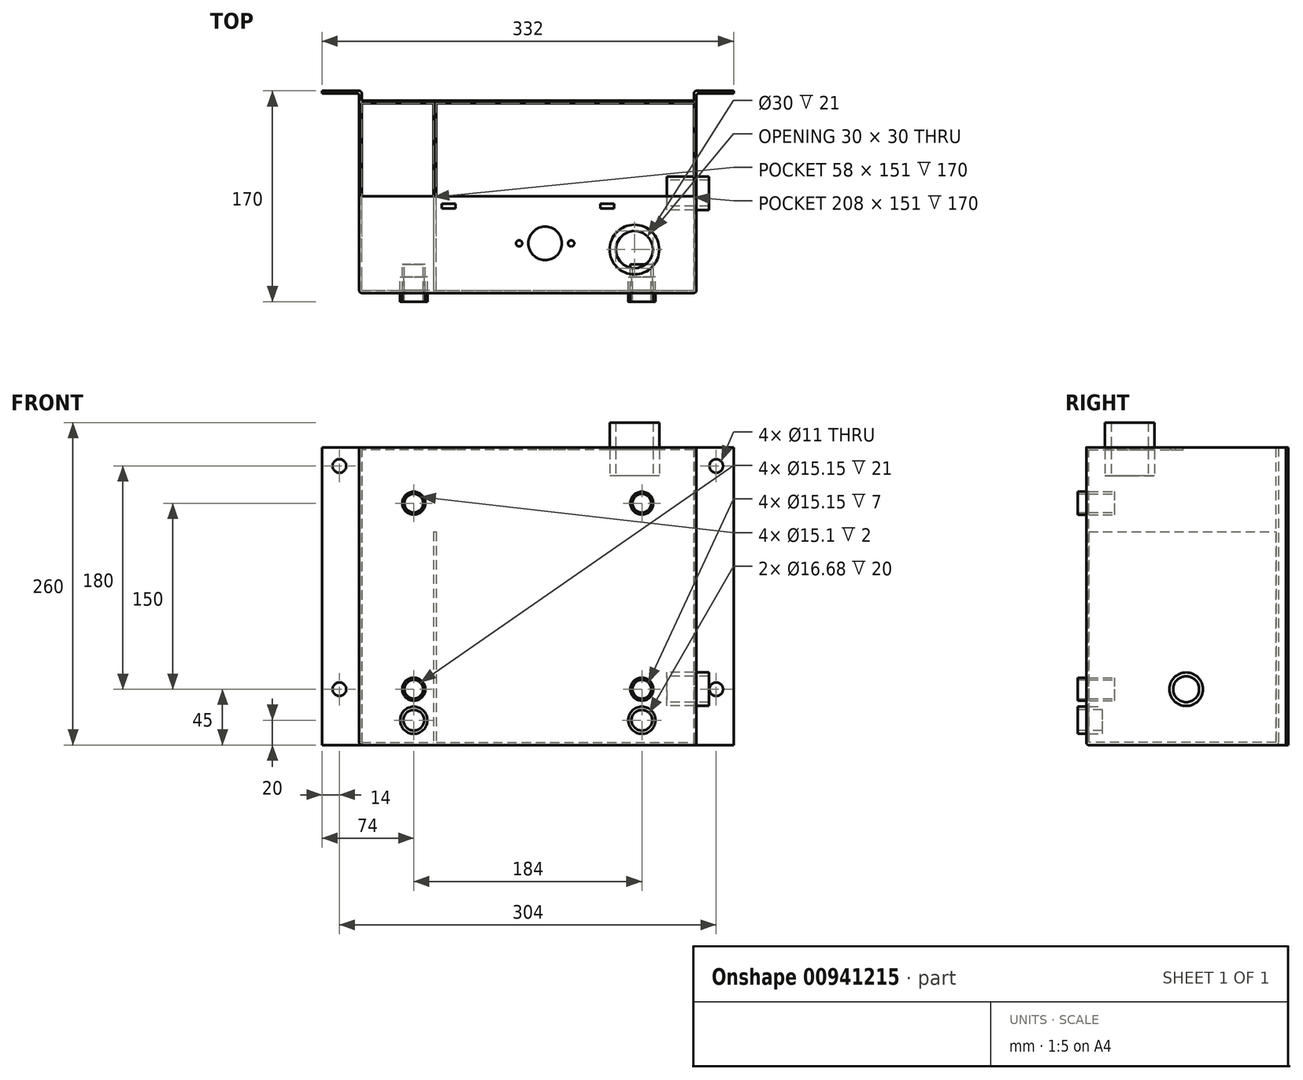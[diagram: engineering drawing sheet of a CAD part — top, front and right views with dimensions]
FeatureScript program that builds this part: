
annotation { "Feature Type Name" : "Feature", "Feature Type Description" : "" }
export const myFeature = defineFeature(function(context is Context, id is Id, definition is map)
    precondition{}
    {
        {
            var Q0;
            Q0=qCreatedBy(makeId("Top.planeOp"),FACE);
            var sketch = newSketch(context, id + "F0", { "sketchPlane" : qUnion([Q0])});
            skLineSegment(sketch, "E0", {"start": v(0, 0) * mm, "end": v(134, 0) * mm});
            skLineSegment(sketch, "E1", {"start": v(136, 0) * mm, "end": v(136, 4) * mm});
            skLineSegment(sketch, "E2", {"start": v(138, 6) * mm, "end": v(166, 6) * mm});
            skPoint(sketch, "E3.visualSharp", {"position": v(136, 6) * mm});
            skArc(sketch, "E3.filletArc", {"start": v(138, 6) * mm, "mid": v(136.59, 5.41) * mm, "end": v(136, 4) * mm});
            skLineSegment(sketch, "E4", {"start": v(136, 0) * mm, "end": v(136, -153) * mm});
            skLineSegment(sketch, "E5", {"start": v(134, -155) * mm, "end": v(0, -155) * mm});
            skPoint(sketch, "E6", {"position": v(0, -2) * mm});
            skLineSegment(sketch, "E7", {"start": v(0, -2) * mm, "end": v(134, -2) * mm});
            skLineSegment(sketch, "E8", {"start": v(134, -2) * mm, "end": v(134, -151) * mm});
            skLineSegment(sketch, "E9", {"start": v(132, -153) * mm, "end": v(0, -153) * mm});
            skLineSegment(sketch, "E10", {"start": v(166, 6) * mm, "end": v(166, 8) * mm});
            skLineSegment(sketch, "E11", {"start": v(134, 0) * mm, "end": v(134, 6) * mm});
            skLineSegment(sketch, "E12", {"start": v(136, 8) * mm, "end": v(166, 8) * mm});
            skPoint(sketch, "E13.visualSharp", {"position": v(134, 8) * mm});
            skArc(sketch, "E13.filletArc", {"start": v(136, 8) * mm, "mid": v(134.59, 7.41) * mm, "end": v(134, 6) * mm});
            skArc(sketch, "E14.MirrorCS", {"start": v(-138, 6) * mm, "mid": v(-136.59, 5.41) * mm, "end": v(-136, 4) * mm});
            skLineSegment(sketch, "E15.MirrorCS", {"start": v(-134, 0) * mm, "end": v(-134, 6) * mm});
            skArc(sketch, "E16.MirrorCS", {"start": v(-136, 8) * mm, "mid": v(-134.59, 7.41) * mm, "end": v(-134, 6) * mm});
            skLineSegment(sketch, "E17.MirrorCS", {"start": v(-136, 0) * mm, "end": v(-136, 4) * mm});
            skLineSegment(sketch, "E18.MirrorCS", {"start": v(-166, 6) * mm, "end": v(-166, 8) * mm});
            skLineSegment(sketch, "E19.MirrorCS", {"start": v(-138, 6) * mm, "end": v(-166, 6) * mm});
            skLineSegment(sketch, "E20.MirrorCS", {"start": v(-134, -2) * mm, "end": v(-134, -151) * mm});
            skLineSegment(sketch, "E21.MirrorCS", {"start": v(-132, -153) * mm, "end": v(0, -153) * mm});
            skPoint(sketch, "E22.MirrorP", {"position": v(-134, 8) * mm});
            skLineSegment(sketch, "E23.MirrorCS", {"start": v(-136, 8) * mm, "end": v(-166, 8) * mm});
            skLineSegment(sketch, "E24.MirrorCS", {"start": v(0, 0) * mm, "end": v(-134, 0) * mm});
            skLineSegment(sketch, "E25.MirrorCS", {"start": v(-134, -155) * mm, "end": v(0, -155) * mm});
            skLineSegment(sketch, "E26.MirrorCS", {"start": v(0, -2) * mm, "end": v(-134, -2) * mm});
            skLineSegment(sketch, "E27.MirrorCS", {"start": v(-136, 0) * mm, "end": v(-136, -153) * mm});
            skPoint(sketch, "E28.visualSharp", {"position": v(-136, -155) * mm});
            skArc(sketch, "E28.filletArc", {"start": v(-136, -153) * mm, "mid": v(-135.41, -154.41) * mm, "end": v(-134, -155) * mm});
            skArc(sketch, "E29.filletArc", {"start": v(-134, -151) * mm, "mid": v(-133.41, -152.41) * mm, "end": v(-132, -153) * mm});
            skPoint(sketch, "E30.visualSharp", {"position": v(136, -155) * mm});
            skArc(sketch, "E30.filletArc", {"start": v(134, -155) * mm, "mid": v(135.41, -154.41) * mm, "end": v(136, -153) * mm});
            skArc(sketch, "E31.filletArc", {"start": v(132, -153) * mm, "mid": v(133.41, -152.41) * mm, "end": v(134, -151) * mm});
            skSolve(sketch);
        }
        {
            var Q0;
            Q0=makeQuery(id+"F0.imprint","IMPRINT",FACE,{"disambiguationData":[TD([[makeQuery(id+"F0.imprint","IMPRINT",EDGE,{"derivedFrom":sQuery(id+"F0.wireOp",EDGE,"E7")}),-1.0]])]});
            var Q1;
            Q1=makeQuery(id+"F0.imprint","IMPRINT",FACE,{"disambiguationData":[TD([[makeQuery(id+"F0.imprint","IMPRINT",EDGE,{"derivedFrom":sQuery(id+"F0.wireOp",EDGE,"E0")}),-1.0]])]});
            var Q2;
            Q2=makeQuery(id+"F0.imprint","IMPRINT",FACE,{"disambiguationData":[TD([[makeQuery(id+"F0.imprint","IMPRINT",EDGE,{"derivedFrom":sQuery(id+"F0.wireOp",EDGE,"AYROce98-IXZU-P0DJ-6LKk-YyaPTNVELOtw")}),1.0]])]});
            extrude(context, id + "F1", {"entities" : qUnion([Q0, Q1, Q2]), "depth" : 240 * mm, "offsetDistance" : 25 * mm});
        }
        {
            var Q0;
            Q0=makeQuery(id+"F1.opExtrude","CAP_FACE",FACE,{"disambiguationData":[OSD([sQuery(id+"F0.wireOp",EDGE,"E0"),sQuery(id+"F0.wireOp",EDGE,"E1"),sQuery(id+"F0.wireOp",EDGE,"E2"),sQuery(id+"F0.wireOp",EDGE,"E3.filletArc"),sQuery(id+"F0.wireOp",EDGE,"E4"),sQuery(id+"F0.wireOp",EDGE,"E5"),sQuery(id+"F0.wireOp",EDGE,"E10"),sQuery(id+"F0.wireOp",EDGE,"E11"),sQuery(id+"F0.wireOp",EDGE,"E12"),sQuery(id+"F0.wireOp",EDGE,"E13.filletArc"),sQuery(id+"F0.wireOp",EDGE,"E14.MirrorCS"),sQuery(id+"F0.wireOp",EDGE,"E15.MirrorCS"),sQuery(id+"F0.wireOp",EDGE,"E16.MirrorCS"),sQuery(id+"F0.wireOp",EDGE,"E17.MirrorCS"),sQuery(id+"F0.wireOp",EDGE,"E18.MirrorCS"),sQuery(id+"F0.wireOp",EDGE,"E19.MirrorCS"),sQuery(id+"F0.wireOp",EDGE,"E23.MirrorCS"),sQuery(id+"F0.wireOp",EDGE,"E24.MirrorCS"),sQuery(id+"F0.wireOp",EDGE,"E25.MirrorCS"),sQuery(id+"F0.wireOp",EDGE,"E27.MirrorCS"),sQuery(id+"F0.wireOp",EDGE,"E28.filletArc"),sQuery(id+"F0.wireOp",EDGE,"E30.filletArc")])],"isStart":false});
            var sketch = newSketch(context, id + "F2", { "sketchPlane" : qUnion([Q0])});
            skPoint(sketch, "E32", {"position": v(-134, -2) * mm});
            skLineSegment(sketch, "E33.bottom", {"start": v(-134, -2) * mm, "end": v(134, -2) * mm});
            skLineSegment(sketch, "E33.top", {"start": v(-134, -153) * mm, "end": v(134, -153) * mm});
            skLineSegment(sketch, "E33.left", {"start": v(-134, -2) * mm, "end": v(-134, -153) * mm});
            skLineSegment(sketch, "E33.right", {"start": v(134, -2) * mm, "end": v(134, -153) * mm});
            skSolve(sketch);
        }
        {
            var Q0;
            Q0=makeQuery(id+"F2.imprint","IMPRINT",FACE,{"disambiguationData":[TD([[makeQuery(id+"F2.imprint","IMPRINT",EDGE,{"derivedFrom":sQuery(id+"F2.wireOp",EDGE,"E33.bottom")}),-1.0]])]});
            extrude(context, id + "F3", {"entities" : qUnion([Q0]), "operationType" : NewBodyOperationType.REMOVE, "oppositeDirection" : true, "depth" : 238 * mm, "offsetDistance" : 25 * mm});
        }
        {
            var Q0;
            Q0=makeQuery(id+"F1.opExtrude","SWEPT_FACE",FACE,{"disambiguationData":[OSD([sQuery(id+"F0.wireOp",EDGE,"E19.MirrorCS")])]});
            var sketch = newSketch(context, id + "F4", { "sketchPlane" : qUnion([Q0])});
            skPoint(sketch, "E34", {"position": v(-152, 45) * mm});
            skPoint(sketch, "E35", {"position": v(-152, 225) * mm});
            skSolve(sketch);
        }
        {
            var Q0;
            Q0=sQuery(id+"F4.wireOp",VERTEX,"E35");
            var Q1;
            Q1=sQuery(id+"F4.wireOp",VERTEX,"E34");
            var Q2;
            Q2=makeQuery(id+"F1.opExtrude","SWEPT_BODY",BODY,{"disambiguationData":[OSD([sQuery(id+"F0.wireOp",EDGE,"E0"),sQuery(id+"F0.wireOp",EDGE,"E1"),sQuery(id+"F0.wireOp",EDGE,"E2"),sQuery(id+"F0.wireOp",EDGE,"E3.filletArc"),sQuery(id+"F0.wireOp",EDGE,"E4"),sQuery(id+"F0.wireOp",EDGE,"E5"),sQuery(id+"F0.wireOp",EDGE,"E10"),sQuery(id+"F0.wireOp",EDGE,"E11"),sQuery(id+"F0.wireOp",EDGE,"E12"),sQuery(id+"F0.wireOp",EDGE,"E13.filletArc"),sQuery(id+"F0.wireOp",EDGE,"E14.MirrorCS"),sQuery(id+"F0.wireOp",EDGE,"E15.MirrorCS"),sQuery(id+"F0.wireOp",EDGE,"E16.MirrorCS"),sQuery(id+"F0.wireOp",EDGE,"E17.MirrorCS"),sQuery(id+"F0.wireOp",EDGE,"E18.MirrorCS"),sQuery(id+"F0.wireOp",EDGE,"E19.MirrorCS"),sQuery(id+"F0.wireOp",EDGE,"E23.MirrorCS"),sQuery(id+"F0.wireOp",EDGE,"E24.MirrorCS"),sQuery(id+"F0.wireOp",EDGE,"E25.MirrorCS"),sQuery(id+"F0.wireOp",EDGE,"E27.MirrorCS"),sQuery(id+"F0.wireOp",EDGE,"E28.filletArc"),sQuery(id+"F0.wireOp",EDGE,"E30.filletArc")])]});
            hole(context, id + "F5", {"style" : HoleStyle.SIMPLE, "endStyle" : HoleEndStyle.THROUGH, "holeDiameter" : 11 * mm, "majorDiameter" : 4 * mm, "isTappedThrough" : true, "tappedDepth" : 5.5 * mm, "tapClearance" : 3, "locations" : qUnion([Q0, Q1]), "scope" : qUnion([Q2])});
        }
        {
            var Q0;
            Q0=makeQuery(id+"F1.opExtrude","SWEPT_FACE",FACE,{"disambiguationData":[OSD([sQuery(id+"F0.wireOp",EDGE,"E2")])]});
            var sketch = newSketch(context, id + "F6", { "sketchPlane" : qUnion([Q0])});
            skPoint(sketch, "E36", {"position": v(152, 225) * mm});
            skPoint(sketch, "E37", {"position": v(152, 45) * mm});
            skSolve(sketch);
        }
        {
            var Q0;
            Q0=sQuery(id+"F6.wireOp",VERTEX,"E36");
            var Q1;
            Q1=sQuery(id+"F6.wireOp",VERTEX,"E37");
            var Q2;
            Q2=makeQuery(id+"F1.opExtrude","SWEPT_BODY",BODY,{"disambiguationData":[OSD([sQuery(id+"F0.wireOp",EDGE,"E0"),sQuery(id+"F0.wireOp",EDGE,"E1"),sQuery(id+"F0.wireOp",EDGE,"E2"),sQuery(id+"F0.wireOp",EDGE,"E3.filletArc"),sQuery(id+"F0.wireOp",EDGE,"E4"),sQuery(id+"F0.wireOp",EDGE,"E5"),sQuery(id+"F0.wireOp",EDGE,"E10"),sQuery(id+"F0.wireOp",EDGE,"E11"),sQuery(id+"F0.wireOp",EDGE,"E12"),sQuery(id+"F0.wireOp",EDGE,"E13.filletArc"),sQuery(id+"F0.wireOp",EDGE,"E14.MirrorCS"),sQuery(id+"F0.wireOp",EDGE,"E15.MirrorCS"),sQuery(id+"F0.wireOp",EDGE,"E16.MirrorCS"),sQuery(id+"F0.wireOp",EDGE,"E17.MirrorCS"),sQuery(id+"F0.wireOp",EDGE,"E18.MirrorCS"),sQuery(id+"F0.wireOp",EDGE,"E19.MirrorCS"),sQuery(id+"F0.wireOp",EDGE,"E23.MirrorCS"),sQuery(id+"F0.wireOp",EDGE,"E24.MirrorCS"),sQuery(id+"F0.wireOp",EDGE,"E25.MirrorCS"),sQuery(id+"F0.wireOp",EDGE,"E27.MirrorCS"),sQuery(id+"F0.wireOp",EDGE,"E28.filletArc"),sQuery(id+"F0.wireOp",EDGE,"E30.filletArc")])]});
            hole(context, id + "F7", {"style" : HoleStyle.SIMPLE, "endStyle" : HoleEndStyle.THROUGH, "holeDiameter" : 11 * mm, "majorDiameter" : 5 * mm, "isTappedThrough" : true, "tappedDepth" : 5.5 * mm, "tapClearance" : 3, "locations" : qUnion([Q0, Q1]), "scope" : qUnion([Q2])});
        }
        {
            var Q0;
            Q0=makeQuery(id+"F1.opExtrude","SWEPT_FACE",FACE,{"disambiguationData":[OSD([sQuery(id+"F0.wireOp",EDGE,"E5"),sQuery(id+"F0.wireOp",EDGE,"E25.MirrorCS")])]});
            var sketch = newSketch(context, id + "F8", { "sketchPlane" : qUnion([Q0])});
            skPoint(sketch, "E38", {"position": v(-92, 195) * mm});
            skPoint(sketch, "E39", {"position": v(-92, 45) * mm});
            skLineSegment(sketch, "E40", {"start": v(0, 240) * mm, "end": v(0, 0) * mm});
            skPoint(sketch, "E41.MirrorP", {"position": v(92, 45) * mm});
            skPoint(sketch, "E42.MirrorP", {"position": v(92, 195) * mm});
            skCircle(sketch, "E43", {"center": v(-92, 195) * mm, "radius": 9.25 * mm});
            skCircle(sketch, "E44", {"center": v(-92, 195) * mm, "radius": 7.58 * mm});
            skCircle(sketch, "E45", {"center": v(-92, 45) * mm, "radius": 9.25 * mm});
            skCircle(sketch, "E46", {"center": v(-92, 45) * mm, "radius": 7.58 * mm});
            skCircle(sketch, "E47", {"center": v(92, 195) * mm, "radius": 9.25 * mm});
            skCircle(sketch, "E48", {"center": v(92, 195) * mm, "radius": 7.58 * mm});
            skCircle(sketch, "E49", {"center": v(92, 45) * mm, "radius": 9.25 * mm});
            skCircle(sketch, "E50", {"center": v(92, 45) * mm, "radius": 7.58 * mm});
            skSolve(sketch);
        }
        {
            var Q0;
            Q0=makeQuery(id+"F8.imprint","IMPRINT",FACE,{"disambiguationData":[TD([[makeQuery(id+"F8.imprint","IMPRINT",EDGE,{"derivedFrom":sQuery(id+"F8.wireOp",EDGE,"E43")}),1.0]])]});
            var Q1;
            Q1=makeQuery(id+"F8.imprint","IMPRINT",FACE,{"disambiguationData":[TD([[makeQuery(id+"F8.imprint","IMPRINT",EDGE,{"derivedFrom":sQuery(id+"F8.wireOp",EDGE,"E45")}),1.0]])]});
            var Q2;
            Q2=makeQuery(id+"F8.imprint","IMPRINT",FACE,{"disambiguationData":[TD([[makeQuery(id+"F8.imprint","IMPRINT",EDGE,{"derivedFrom":sQuery(id+"F8.wireOp",EDGE,"E47")}),1.0]])]});
            var Q3;
            Q3=makeQuery(id+"F8.imprint","IMPRINT",FACE,{"disambiguationData":[TD([[makeQuery(id+"F8.imprint","IMPRINT",EDGE,{"derivedFrom":sQuery(id+"F8.wireOp",EDGE,"E49")}),1.0]])]});
            extrude(context, id + "F9", {"entities" : qUnion([Q0, Q1, Q2, Q3]), "operationType" : NewBodyOperationType.ADD, "depth" : 7 * mm, "offsetDistance" : 25 * mm, "hasSecondDirection" : true, "secondDirectionOppositeDirection" : true, "secondDirectionDepth" : 23 * mm});
        }
        {
            var Q0;
            {var subQ1=sQuery(id+"F0.wireOp",EDGE,"E28.filletArc");var subQ3=sQuery(id+"F0.wireOp",EDGE,"E25.MirrorCS");var subQ16=sQuery(id+"F0.wireOp",EDGE,"E5");Q0=makeQuery(id+"F9.boolean.opBoolean","SPLIT",FACE,{"disambiguationData":[TD([makeQuery(id+"F1.opExtrude","SWEPT_FACE",FACE,{"disambiguationData":[OSD([subQ1])]})])],"derivedFrom":makeQuery(id+"F1.opExtrude","SWEPT_FACE",FACE,{"disambiguationData":[OSD([subQ16,subQ3])]})});}
            var sketch = newSketch(context, id + "F10", { "sketchPlane" : qUnion([Q0])});
            skCircle(sketch, "E51", {"center": v(-92, 195) * mm, "radius": 7.55 * mm});
            skCircle(sketch, "E52", {"center": v(-92, 45) * mm, "radius": 7.55 * mm});
            skCircle(sketch, "E53", {"center": v(92, 195) * mm, "radius": 7.55 * mm});
            skCircle(sketch, "E54", {"center": v(92, 45) * mm, "radius": 7.55 * mm});
            skSolve(sketch);
        }
        {
            var Q0;
            Q0=makeQuery(id+"F10.imprint","IMPRINT",FACE,{"disambiguationData":[TD([[makeQuery(id+"F10.imprint","IMPRINT",EDGE,{"derivedFrom":sQuery(id+"F10.wireOp",EDGE,"E51")}),1.0]])]});
            var Q1;
            Q1=makeQuery(id+"F10.imprint","IMPRINT",FACE,{"disambiguationData":[TD([[makeQuery(id+"F10.imprint","IMPRINT",EDGE,{"derivedFrom":sQuery(id+"F10.wireOp",EDGE,"E52")}),1.0]])]});
            var Q2;
            Q2=makeQuery(id+"F10.imprint","IMPRINT",FACE,{"disambiguationData":[TD([[makeQuery(id+"F10.imprint","IMPRINT",EDGE,{"derivedFrom":sQuery(id+"F10.wireOp",EDGE,"E54")}),1.0]])]});
            var Q3;
            Q3=makeQuery(id+"F10.imprint","IMPRINT",FACE,{"disambiguationData":[TD([[makeQuery(id+"F10.imprint","IMPRINT",EDGE,{"derivedFrom":sQuery(id+"F10.wireOp",EDGE,"E53")}),1.0]])]});
            extrude(context, id + "F11", {"entities" : qUnion([Q0, Q1, Q2, Q3]), "operationType" : NewBodyOperationType.REMOVE, "oppositeDirection" : true, "depth" : 25 * mm, "offsetDistance" : 25 * mm});
        }
        {
            var Q0;
            Q0=makeQuery(id+"F1.opExtrude","SWEPT_FACE",FACE,{"disambiguationData":[OSD([sQuery(id+"F0.wireOp",EDGE,"E1"),sQuery(id+"F0.wireOp",EDGE,"E4")])]});
            var sketch = newSketch(context, id + "F12", { "sketchPlane" : qUnion([Q0])});
            skPoint(sketch, "E55.endSnap0", {"position": v(-74.5, 0) * mm});
            skCircle(sketch, "E56", {"center": v(-74.5, 45) * mm, "radius": 13.5 * mm});
            skCircle(sketch, "E57", {"center": v(-74.5, 45) * mm, "radius": 10.48 * mm});
            skSolve(sketch);
        }
        {
            var Q0;
            Q0=makeQuery(id+"F12.imprint","IMPRINT",FACE,{"disambiguationData":[TD([[makeQuery(id+"F12.imprint","IMPRINT",EDGE,{"derivedFrom":sQuery(id+"F12.wireOp",EDGE,"E56")}),1.0]])]});
            extrude(context, id + "F13", {"entities" : qUnion([Q0]), "operationType" : NewBodyOperationType.ADD, "depth" : 10 * mm, "offsetDistance" : 25 * mm, "hasSecondDirection" : true, "secondDirectionOppositeDirection" : true, "secondDirectionDepth" : 24 * mm});
        }
        {
            var Q0;
            {var subQ17=sQuery(id+"F0.wireOp",EDGE,"E4");var subQ18=sQuery(id+"F0.wireOp",EDGE,"E3.filletArc");var subQ20=sQuery(id+"F0.wireOp",EDGE,"E1");Q0=makeQuery(id+"F13.boolean.opBoolean","SPLIT",FACE,{"disambiguationData":[TD([makeQuery(id+"F1.opExtrude","SWEPT_FACE",FACE,{"disambiguationData":[OSD([subQ18])]})])],"derivedFrom":makeQuery(id+"F1.opExtrude","SWEPT_FACE",FACE,{"disambiguationData":[OSD([subQ20,subQ17])]})});}
            var sketch = newSketch(context, id + "F14", { "sketchPlane" : qUnion([Q0])});
            skCircle(sketch, "E58", {"center": v(-74.5, 45) * mm, "radius": 10.47 * mm});
            skSolve(sketch);
        }
        {
            var Q0;
            Q0=makeQuery(id+"F14.imprint","IMPRINT",FACE,{"disambiguationData":[TD([[makeQuery(id+"F14.imprint","IMPRINT",EDGE,{"derivedFrom":sQuery(id+"F14.wireOp",EDGE,"E58")}),1.0]])]});
            extrude(context, id + "F15", {"entities" : qUnion([Q0]), "operationType" : NewBodyOperationType.REMOVE, "oppositeDirection" : true, "depth" : 25 * mm, "offsetDistance" : 25 * mm});
        }
        {
            var Q0;
            Q0=makeQuery(id+"F3.boolean.opBoolean","COPY",FACE,{"derivedFrom":makeQuery(id+"F3.opExtrude","CAP_FACE",FACE,{"disambiguationData":[OSD([sQuery(id+"F2.wireOp",EDGE,"E33.bottom"),sQuery(id+"F2.wireOp",EDGE,"E33.top"),sQuery(id+"F2.wireOp",EDGE,"E33.left"),sQuery(id+"F2.wireOp",EDGE,"E33.right")])],"isStart":false})});
            var sketch = newSketch(context, id + "F16", { "sketchPlane" : qUnion([Q0])});
            skPoint(sketch, "E59", {"position": v(-74, -2) * mm});
            skPoint(sketch, "E60", {"position": v(-74, -153) * mm});
            skLineSegment(sketch, "E61", {"start": v(-74, -153) * mm, "end": v(-74, -2) * mm});
            skLineSegment(sketch, "E62", {"start": v(-76, -2) * mm, "end": v(-76, -153) * mm});
            skLineSegment(sketch, "E63", {"start": v(-76, -153) * mm, "end": v(-74, -153) * mm});
            skLineSegment(sketch, "E64", {"start": v(-76, -2) * mm, "end": v(-74, -2) * mm});
            skSolve(sketch);
        }
        {
            var Q0;
            Q0=makeQuery(id+"F16.imprint","IMPRINT",FACE,{"disambiguationData":[TD([[makeQuery(id+"F16.imprint","IMPRINT",EDGE,{"derivedFrom":sQuery(id+"F16.wireOp",EDGE,"E61")}),1.0]])]});
            extrude(context, id + "F17", {"entities" : qUnion([Q0]), "operationType" : NewBodyOperationType.ADD, "depth" : 170 * mm, "offsetDistance" : 25 * mm});
        }
        {
            var Q0;
            Q0=makeQuery(id+"F3.boolean.opBoolean","COPY",FACE,{"derivedFrom":makeQuery(id+"F3.opExtrude","SWEPT_FACE",FACE,{"disambiguationData":[OSD([sQuery(id+"F2.wireOp",EDGE,"E33.bottom")])]})});
            var sketch = newSketch(context, id + "F18", { "sketchPlane" : qUnion([Q0])});
            skLineSegment(sketch, "E65", {"start": v(-134, 240) * mm, "end": v(-134, 238) * mm});
            skLineSegment(sketch, "E66", {"start": v(-134, 238) * mm, "end": v(134, 238) * mm});
            skLineSegment(sketch, "E67", {"start": v(134, 238) * mm, "end": v(134, 240) * mm});
            skLineSegment(sketch, "E68", {"start": v(134, 240) * mm, "end": v(-134, 240) * mm});
            skSolve(sketch);
        }
        {
            var Q0;
            Q0=makeQuery(id+"F18.imprint","IMPRINT",FACE,{"disambiguationData":[TD([[makeQuery(id+"F18.imprint","IMPRINT",EDGE,{"derivedFrom":sQuery(id+"F18.wireOp",EDGE,"E65")}),-1.0]])]});
            extrude(context, id + "F19", {"entities" : qUnion([Q0]), "operationType" : NewBodyOperationType.ADD, "endBound" : BoundingType.UP_TO_NEXT, "depth" : 25 * mm, "offsetDistance" : 25 * mm});
        }
        {
            var Q0;
            Q0=makeQuery(id+"F1.opExtrude","CAP_EDGE",EDGE,{"disambiguationData":[OSD([sQuery(id+"F0.wireOp",EDGE,"E0"),sQuery(id+"F0.wireOp",EDGE,"E24.MirrorCS")])],"isStart":true});
            fillet(context, id + "F20", {"entities" : qUnion([Q0]), "radius" : 2 * mm, "tangentPropagation" : true, "allowEdgeOverflow" : false});
        }
        {
            var Q0;
            Q0=makeQuery(id+"F1.opExtrude","CAP_EDGE",EDGE,{"disambiguationData":[OSD([sQuery(id+"F0.wireOp",EDGE,"E5"),sQuery(id+"F0.wireOp",EDGE,"E25.MirrorCS")])],"isStart":true});
            fillet(context, id + "F21", {"entities" : qUnion([Q0]), "radius" : 2 * mm, "tangentPropagation" : true, "allowEdgeOverflow" : false});
        }
        {
            var Q0;
            Q0=makeQuery(id+"F19.boolean.opBoolean","MERGE",FACE,{"derivedFrom":[makeQuery(id+"F1.opExtrude","CAP_FACE",FACE,{"disambiguationData":[OSD([sQuery(id+"F0.wireOp",EDGE,"E0"),sQuery(id+"F0.wireOp",EDGE,"E1"),sQuery(id+"F0.wireOp",EDGE,"E2"),sQuery(id+"F0.wireOp",EDGE,"E3.filletArc"),sQuery(id+"F0.wireOp",EDGE,"E4"),sQuery(id+"F0.wireOp",EDGE,"E5"),sQuery(id+"F0.wireOp",EDGE,"E10"),sQuery(id+"F0.wireOp",EDGE,"E11"),sQuery(id+"F0.wireOp",EDGE,"E12"),sQuery(id+"F0.wireOp",EDGE,"E13.filletArc"),sQuery(id+"F0.wireOp",EDGE,"E14.MirrorCS"),sQuery(id+"F0.wireOp",EDGE,"E15.MirrorCS"),sQuery(id+"F0.wireOp",EDGE,"E16.MirrorCS"),sQuery(id+"F0.wireOp",EDGE,"E17.MirrorCS"),sQuery(id+"F0.wireOp",EDGE,"E18.MirrorCS"),sQuery(id+"F0.wireOp",EDGE,"E19.MirrorCS"),sQuery(id+"F0.wireOp",EDGE,"E23.MirrorCS"),sQuery(id+"F0.wireOp",EDGE,"E24.MirrorCS"),sQuery(id+"F0.wireOp",EDGE,"E25.MirrorCS"),sQuery(id+"F0.wireOp",EDGE,"E27.MirrorCS"),sQuery(id+"F0.wireOp",EDGE,"E28.filletArc"),sQuery(id+"F0.wireOp",EDGE,"E30.filletArc")])],"isStart":false}),makeQuery(id+"F19.opExtrude","SWEPT_FACE",FACE,{"disambiguationData":[OSD([sQuery(id+"F18.wireOp",EDGE,"E68")])]})]});
            var sketch = newSketch(context, id + "F22", { "sketchPlane" : qUnion([Q0])});
            skLineSegment(sketch, "E69", {"start": v(-134, -2) * mm, "end": v(-134, -77) * mm});
            skLineSegment(sketch, "E70", {"start": v(-134, -77) * mm, "end": v(134, -77) * mm});
            skLineSegment(sketch, "E71", {"start": v(134, -77) * mm, "end": v(134, -2) * mm});
            skLineSegment(sketch, "E72", {"start": v(134, -2) * mm, "end": v(-134, -2) * mm});
            skSolve(sketch);
        }
        {
            var Q0;
            Q0=makeQuery(id+"F22.imprint","IMPRINT",FACE,{"disambiguationData":[TD([[makeQuery(id+"F22.imprint","IMPRINT",EDGE,{"derivedFrom":sQuery(id+"F22.wireOp",EDGE,"E69")}),1.0]])]});
            extrude(context, id + "F23", {"entities" : qUnion([Q0]), "operationType" : NewBodyOperationType.REMOVE, "endBound" : BoundingType.UP_TO_NEXT, "oppositeDirection" : true, "depth" : 25 * mm, "offsetDistance" : 25 * mm});
        }
        {
            var Q0;
            Q0=makeQuery(id+"F19.boolean.opBoolean","MERGE",FACE,{"derivedFrom":[makeQuery(id+"F1.opExtrude","CAP_FACE",FACE,{"disambiguationData":[OSD([sQuery(id+"F0.wireOp",EDGE,"E0"),sQuery(id+"F0.wireOp",EDGE,"E1"),sQuery(id+"F0.wireOp",EDGE,"E2"),sQuery(id+"F0.wireOp",EDGE,"E3.filletArc"),sQuery(id+"F0.wireOp",EDGE,"E4"),sQuery(id+"F0.wireOp",EDGE,"E5"),sQuery(id+"F0.wireOp",EDGE,"E10"),sQuery(id+"F0.wireOp",EDGE,"E11"),sQuery(id+"F0.wireOp",EDGE,"E12"),sQuery(id+"F0.wireOp",EDGE,"E13.filletArc"),sQuery(id+"F0.wireOp",EDGE,"E14.MirrorCS"),sQuery(id+"F0.wireOp",EDGE,"E15.MirrorCS"),sQuery(id+"F0.wireOp",EDGE,"E16.MirrorCS"),sQuery(id+"F0.wireOp",EDGE,"E17.MirrorCS"),sQuery(id+"F0.wireOp",EDGE,"E18.MirrorCS"),sQuery(id+"F0.wireOp",EDGE,"E19.MirrorCS"),sQuery(id+"F0.wireOp",EDGE,"E23.MirrorCS"),sQuery(id+"F0.wireOp",EDGE,"E24.MirrorCS"),sQuery(id+"F0.wireOp",EDGE,"E25.MirrorCS"),sQuery(id+"F0.wireOp",EDGE,"E27.MirrorCS"),sQuery(id+"F0.wireOp",EDGE,"E28.filletArc"),sQuery(id+"F0.wireOp",EDGE,"E30.filletArc")])],"isStart":false}),makeQuery(id+"F19.opExtrude","SWEPT_FACE",FACE,{"disambiguationData":[OSD([sQuery(id+"F18.wireOp",EDGE,"E68")])]})]});
            var sketch = newSketch(context, id + "F24", { "sketchPlane" : qUnion([Q0])});
            skPoint(sketch, "E73", {"position": v(14, -115) * mm});
            skCircle(sketch, "E74", {"center": v(14, -115) * mm, "radius": 13.5 * mm});
            skSolve(sketch);
        }
        {
            var Q0;
            Q0=makeQuery(id+"F24.imprint","IMPRINT",FACE,{"disambiguationData":[TD([[makeQuery(id+"F24.imprint","IMPRINT",EDGE,{"derivedFrom":sQuery(id+"F24.wireOp",EDGE,"E74")}),1.0]])]});
            extrude(context, id + "F25", {"entities" : qUnion([Q0]), "operationType" : NewBodyOperationType.REMOVE, "oppositeDirection" : true, "depth" : 25 * mm, "offsetDistance" : 25 * mm});
        }
        {
            var Q0;
            Q0=makeQuery(id+"F19.boolean.opBoolean","MERGE",FACE,{"derivedFrom":[makeQuery(id+"F1.opExtrude","CAP_FACE",FACE,{"disambiguationData":[OSD([sQuery(id+"F0.wireOp",EDGE,"E0"),sQuery(id+"F0.wireOp",EDGE,"E1"),sQuery(id+"F0.wireOp",EDGE,"E2"),sQuery(id+"F0.wireOp",EDGE,"E3.filletArc"),sQuery(id+"F0.wireOp",EDGE,"E4"),sQuery(id+"F0.wireOp",EDGE,"E5"),sQuery(id+"F0.wireOp",EDGE,"E10"),sQuery(id+"F0.wireOp",EDGE,"E11"),sQuery(id+"F0.wireOp",EDGE,"E12"),sQuery(id+"F0.wireOp",EDGE,"E13.filletArc"),sQuery(id+"F0.wireOp",EDGE,"E14.MirrorCS"),sQuery(id+"F0.wireOp",EDGE,"E15.MirrorCS"),sQuery(id+"F0.wireOp",EDGE,"E16.MirrorCS"),sQuery(id+"F0.wireOp",EDGE,"E17.MirrorCS"),sQuery(id+"F0.wireOp",EDGE,"E18.MirrorCS"),sQuery(id+"F0.wireOp",EDGE,"E19.MirrorCS"),sQuery(id+"F0.wireOp",EDGE,"E23.MirrorCS"),sQuery(id+"F0.wireOp",EDGE,"E24.MirrorCS"),sQuery(id+"F0.wireOp",EDGE,"E25.MirrorCS"),sQuery(id+"F0.wireOp",EDGE,"E27.MirrorCS"),sQuery(id+"F0.wireOp",EDGE,"E28.filletArc"),sQuery(id+"F0.wireOp",EDGE,"E30.filletArc")])],"isStart":false}),makeQuery(id+"F19.opExtrude","SWEPT_FACE",FACE,{"disambiguationData":[OSD([sQuery(id+"F18.wireOp",EDGE,"E68")])]})]});
            var sketch = newSketch(context, id + "F26", { "sketchPlane" : qUnion([Q0])});
            skPoint(sketch, "E75", {"position": v(-134, 0) * mm});
            skPoint(sketch, "E76", {"position": v(-64, -85) * mm});
            skPoint(sketch, "E77", {"position": v(64, -85) * mm});
            skLineSegment(sketch, "E78.bottom", {"start": v(-58.5, -87) * mm, "end": v(-69.5, -87) * mm});
            skLineSegment(sketch, "E78.top", {"start": v(-58.5, -83) * mm, "end": v(-69.5, -83) * mm});
            skLineSegment(sketch, "E78.left", {"start": v(-58.5, -87) * mm, "end": v(-58.5, -83) * mm});
            skLineSegment(sketch, "E78.right", {"start": v(-69.5, -87) * mm, "end": v(-69.5, -83) * mm});
            skLineSegment(sketch, "E79.bottom", {"start": v(69.5, -87) * mm, "end": v(58.5, -87) * mm});
            skLineSegment(sketch, "E79.top", {"start": v(69.5, -83) * mm, "end": v(58.5, -83) * mm});
            skLineSegment(sketch, "E79.left", {"start": v(69.5, -87) * mm, "end": v(69.5, -83) * mm});
            skLineSegment(sketch, "E79.right", {"start": v(58.5, -87) * mm, "end": v(58.5, -83) * mm});
            skSolve(sketch);
        }
        {
            var Q0;
            Q0=makeQuery(id+"F26.imprint","IMPRINT",FACE,{"disambiguationData":[TD([[makeQuery(id+"F26.imprint","IMPRINT",EDGE,{"derivedFrom":sQuery(id+"F26.wireOp",EDGE,"E78.bottom")}),-1.0]])]});
            var Q1;
            Q1=makeQuery(id+"F26.imprint","IMPRINT",FACE,{"disambiguationData":[TD([[makeQuery(id+"F26.imprint","IMPRINT",EDGE,{"derivedFrom":sQuery(id+"F26.wireOp",EDGE,"E79.bottom")}),-1.0]])]});
            extrude(context, id + "F27", {"entities" : qUnion([Q0, Q1]), "operationType" : NewBodyOperationType.REMOVE, "oppositeDirection" : true, "depth" : 5 * mm, "offsetDistance" : 25 * mm});
        }
        {
            var Q0;
            {var subQ1=sQuery(id+"F0.wireOp",EDGE,"E28.filletArc");var subQ3=sQuery(id+"F0.wireOp",EDGE,"E25.MirrorCS");var subQ16=sQuery(id+"F0.wireOp",EDGE,"E5");Q0=makeQuery(id+"F9.boolean.opBoolean","SPLIT",FACE,{"disambiguationData":[TD([makeQuery(id+"F1.opExtrude","SWEPT_FACE",FACE,{"disambiguationData":[OSD([subQ1])]})])],"derivedFrom":makeQuery(id+"F1.opExtrude","SWEPT_FACE",FACE,{"disambiguationData":[OSD([subQ16,subQ3])]})});}
            var sketch = newSketch(context, id + "F28", { "sketchPlane" : qUnion([Q0])});
            skLineSegment(sketch, "E80", {"start": v(-92, 195) * mm, "end": v(-92, 28.34) * mm});
            skLineSegment(sketch, "E81", {"start": v(92, 195) * mm, "end": v(92, 28.34) * mm});
            skPoint(sketch, "E82", {"position": v(-92, 20) * mm});
            skPoint(sketch, "E83", {"position": v(92, 20) * mm});
            skCircle(sketch, "E84", {"center": v(-92, 20) * mm, "radius": 8.34 * mm});
            skCircle(sketch, "E85", {"center": v(92, 20) * mm, "radius": 8.34 * mm});
            skLineSegment(sketch, "E86.trimOffspring", {"start": v(-92, 11.66) * mm, "end": v(-92, 2) * mm});
            skLineSegment(sketch, "E87.trimOffspring", {"start": v(92, 11.66) * mm, "end": v(92, 2) * mm});
            skSolve(sketch);
        }
        {
            var Q0;
            {var subQ0=sQuery(id+"F28.wireOp",EDGE,"E84");var subQ1=makeQuery(id+"F28.imprint","IMPRINT",VERTEX,{"disambiguationData":[OD(0.0)],"derivedFrom":subQ0});Q0=makeQuery(id+"F28.imprint","IMPRINT",FACE,{"disambiguationData":[TD([[makeQuery(id+"F28.imprint","IMPRINT",EDGE,{"disambiguationData":[TD([[subQ1,-1.0]])],"derivedFrom":subQ0}),1.0]])]});}
            var Q1;
            {var subQ0=sQuery(id+"F28.wireOp",EDGE,"E85");var subQ1=makeQuery(id+"F28.imprint","IMPRINT",VERTEX,{"disambiguationData":[OD(0.0)],"derivedFrom":subQ0});Q1=makeQuery(id+"F28.imprint","IMPRINT",FACE,{"disambiguationData":[TD([[makeQuery(id+"F28.imprint","IMPRINT",EDGE,{"disambiguationData":[TD([[subQ1,-1.0]])],"derivedFrom":subQ0}),1.0]])]});}
            extrude(context, id + "F29", {"entities" : qUnion([Q0, Q1]), "operationType" : NewBodyOperationType.REMOVE, "oppositeDirection" : true, "depth" : 25 * mm, "offsetDistance" : 25 * mm});
        }
        {
            var Q0;
            Q0=makeQuery(id+"F2.imprint","IMPRINT",FACE,{"disambiguationData":[TD([[makeQuery(id+"F2.imprint","IMPRINT",EDGE,{"derivedFrom":sQuery(id+"F2.wireOp",EDGE,"E33.bottom")}),-1.0]])]});
            var sketch = newSketch(context, id + "F30", { "sketchPlane" : qUnion([Q0])});
            skLineSegment(sketch, "E88", {"start": v(0, 0) * mm, "end": v(0, -190) * mm});
            skPoint(sketch, "E89", {"position": v(86, -120) * mm});
            skCircle(sketch, "E90", {"center": v(86, -120) * mm, "radius": 20 * mm});
            skCircle(sketch, "E91", {"center": v(86, -120) * mm, "radius": 15 * mm});
            skSolve(sketch);
        }
        {
            var Q0;
            Q0=makeQuery(id+"F30.imprint","IMPRINT",FACE,{"disambiguationData":[TD([[makeQuery(id+"F30.imprint","IMPRINT",EDGE,{"derivedFrom":sQuery(id+"F30.wireOp",EDGE,"E90")}),1.0]])]});
            extrude(context, id + "F31", {"entities" : qUnion([Q0]), "operationType" : NewBodyOperationType.ADD, "depth" : 20 * mm, "offsetDistance" : 25 * mm, "hasSecondDirection" : true, "secondDirectionOppositeDirection" : true, "secondDirectionDepth" : 23 * mm});
        }
        {
            var Q0;
            Q0=makeQuery(id+"F31.opExtrude","CAP_FACE",FACE,{"disambiguationData":[OSD([sQuery(id+"F30.wireOp",EDGE,"E90"),sQuery(id+"F30.wireOp",EDGE,"E91")])],"isStart":false});
            var sketch = newSketch(context, id + "F32", { "sketchPlane" : qUnion([Q0])});
            skCircle(sketch, "E92", {"center": v(86, -120) * mm, "radius": 15 * mm});
            skSolve(sketch);
        }
        {
            var Q0;
            Q0=makeQuery(id+"F32.imprint","IMPRINT",FACE,{"disambiguationData":[TD([[makeQuery(id+"F32.imprint","IMPRINT",EDGE,{"derivedFrom":sQuery(id+"F32.wireOp",EDGE,"E92")}),1.0]])]});
            extrude(context, id + "F33", {"entities" : qUnion([Q0]), "operationType" : NewBodyOperationType.REMOVE, "oppositeDirection" : true, "depth" : 50 * mm, "offsetDistance" : 25 * mm});
        }
        {
            var Q0;
            Q0=makeQuery(id+"F2.imprint","IMPRINT",FACE,{"disambiguationData":[TD([[makeQuery(id+"F2.imprint","IMPRINT",EDGE,{"derivedFrom":sQuery(id+"F2.wireOp",EDGE,"E33.bottom")}),-1.0]])]});
            var sketch = newSketch(context, id + "F34", { "sketchPlane" : qUnion([Q0])});
            skPoint(sketch, "E93", {"position": v(35, -115) * mm});
            skPoint(sketch, "E94", {"position": v(-7, -115) * mm});
            skSolve(sketch);
        }
        {
            var Q0;
            Q0=sQuery(id+"F34.wireOp",VERTEX,"E93");
            var Q1;
            Q1=sQuery(id+"F34.wireOp",VERTEX,"E94");
            var Q2;
            Q2=makeQuery(id+"F1.opExtrude","SWEPT_BODY",BODY,{"disambiguationData":[OSD([sQuery(id+"F0.wireOp",EDGE,"E0"),sQuery(id+"F0.wireOp",EDGE,"E1"),sQuery(id+"F0.wireOp",EDGE,"E2"),sQuery(id+"F0.wireOp",EDGE,"E3.filletArc"),sQuery(id+"F0.wireOp",EDGE,"E4"),sQuery(id+"F0.wireOp",EDGE,"E5"),sQuery(id+"F0.wireOp",EDGE,"E10"),sQuery(id+"F0.wireOp",EDGE,"E11"),sQuery(id+"F0.wireOp",EDGE,"E12"),sQuery(id+"F0.wireOp",EDGE,"E13.filletArc"),sQuery(id+"F0.wireOp",EDGE,"E14.MirrorCS"),sQuery(id+"F0.wireOp",EDGE,"E15.MirrorCS"),sQuery(id+"F0.wireOp",EDGE,"E16.MirrorCS"),sQuery(id+"F0.wireOp",EDGE,"E17.MirrorCS"),sQuery(id+"F0.wireOp",EDGE,"E18.MirrorCS"),sQuery(id+"F0.wireOp",EDGE,"E19.MirrorCS"),sQuery(id+"F0.wireOp",EDGE,"E23.MirrorCS"),sQuery(id+"F0.wireOp",EDGE,"E24.MirrorCS"),sQuery(id+"F0.wireOp",EDGE,"E25.MirrorCS"),sQuery(id+"F0.wireOp",EDGE,"E27.MirrorCS"),sQuery(id+"F0.wireOp",EDGE,"E28.filletArc"),sQuery(id+"F0.wireOp",EDGE,"E30.filletArc")])]});
            hole(context, id + "F35", {"style" : HoleStyle.SIMPLE, "endStyle" : HoleEndStyle.BLIND, "standardTappedOrClearance" : lookupTablePath({ "standard" : "ISO", "engagement" : "75%", "pitch" : "1 mm", "size" : "M6", "type" : "Tapped" }), "standardBlindInLast" : lookupTablePath({ "standard" : "ISO", "fit" : "Normal", "engagement" : "75%", "pitch" : "1 mm", "size" : "M6", "type" : "Clearance & tapped" }), "holeDiameter" : 5 * mm, "majorDiameter" : 6 * mm, "showTappedDepth" : true, "holeDepth" : 8.5 * mm, "isTappedThrough" : true, "tappedDepth" : 5.5 * mm, "tapClearance" : 3, "locations" : qUnion([Q0, Q1]), "scope" : qUnion([Q2])});
        }
        {
            var Q0;
            {var subQ1=sQuery(id+"F0.wireOp",EDGE,"E28.filletArc");var subQ3=sQuery(id+"F0.wireOp",EDGE,"E25.MirrorCS");var subQ16=sQuery(id+"F0.wireOp",EDGE,"E5");Q0=makeQuery(id+"F9.boolean.opBoolean","SPLIT",FACE,{"disambiguationData":[TD([makeQuery(id+"F1.opExtrude","SWEPT_FACE",FACE,{"disambiguationData":[OSD([subQ1])]})])],"derivedFrom":makeQuery(id+"F1.opExtrude","SWEPT_FACE",FACE,{"disambiguationData":[OSD([subQ16,subQ3])]})});}
            var sketch = newSketch(context, id + "F36", { "sketchPlane" : qUnion([Q0])});
            skCircle(sketch, "E95", {"center": v(-92, 20) * mm, "radius": 11 * mm});
            skCircle(sketch, "E96", {"center": v(92, 20) * mm, "radius": 11 * mm});
            skCircle(sketch, "E97", {"center": v(-92, 20) * mm, "radius": 8.34 * mm});
            skCircle(sketch, "E98", {"center": v(92, 20) * mm, "radius": 8.34 * mm});
            skSolve(sketch);
        }
        {
            var Q0;
            Q0=makeQuery(id+"F36.imprint","IMPRINT",FACE,{"disambiguationData":[TD([[makeQuery(id+"F36.imprint","IMPRINT",EDGE,{"derivedFrom":sQuery(id+"F36.wireOp",EDGE,"E95")}),1.0]])]});
            var Q1;
            Q1=makeQuery(id+"F36.imprint","IMPRINT",FACE,{"disambiguationData":[TD([[makeQuery(id+"F36.imprint","IMPRINT",EDGE,{"derivedFrom":sQuery(id+"F36.wireOp",EDGE,"E96")}),1.0]])]});
            extrude(context, id + "F37", {"entities" : qUnion([Q0, Q1]), "operationType" : NewBodyOperationType.ADD, "depth" : 7 * mm, "offsetDistance" : 25 * mm, "hasSecondDirection" : true, "secondDirectionOppositeDirection" : true, "secondDirectionDepth" : 13 * mm});
        }
    });
